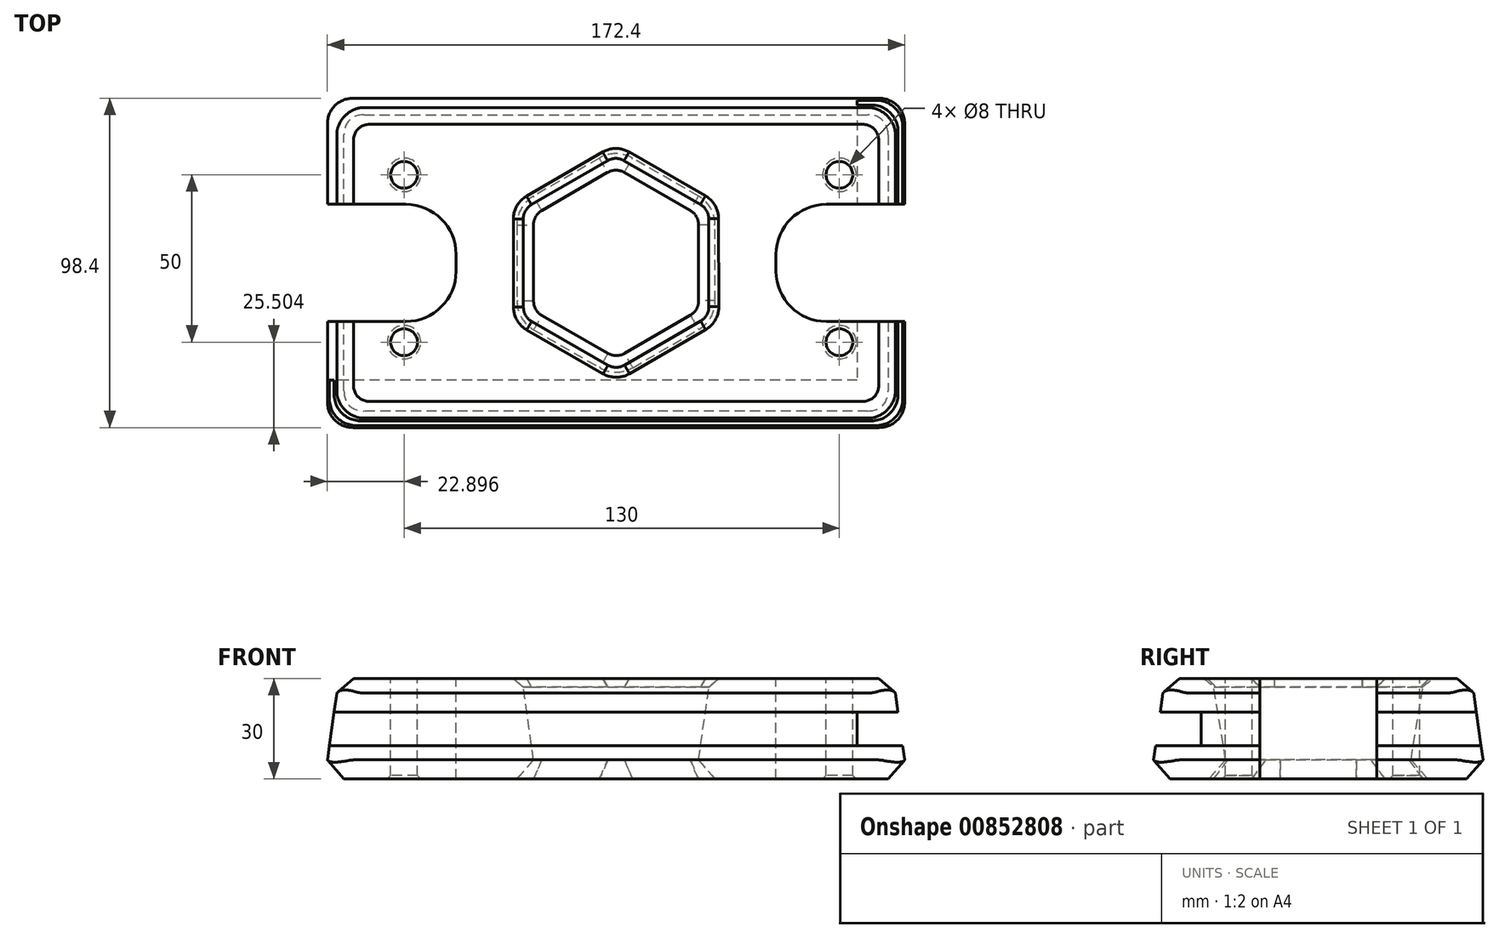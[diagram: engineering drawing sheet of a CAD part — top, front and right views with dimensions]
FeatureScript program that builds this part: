
annotation { "Feature Type Name" : "Feature", "Feature Type Description" : "" }
export const myFeature = defineFeature(function(context is Context, id is Id, definition is map)
    precondition{}
    {
        {
            var Q0;
            Q0=qCreatedBy(makeId("Top.planeOp"),FACE);
            var sketch = newSketch(context, id + "F0", { "sketchPlane" : qUnion([Q0])});
            skLineSegment(sketch, "E0.bottom", {"start": v(87, 50) * mm, "end": v(-87, 50) * mm});
            skLineSegment(sketch, "E0.top", {"start": v(87, -50) * mm, "end": v(-87, -50) * mm});
            skLineSegment(sketch, "E0.left", {"start": v(87, 50) * mm, "end": v(87, -50) * mm});
            skLineSegment(sketch, "E0.right", {"start": v(-87, 50) * mm, "end": v(-87, -50) * mm});
            skPoint(sketch, "E0.middle", {"position": v(0, 0) * mm});
            skCircle(sketch, "E1.cCircle", {"center": v(0, 0) * mm, "radius": 23.84 * mm, "construction": true});
            skLineSegment(sketch, "E1.0", {"start": v(-0.05, 27.52) * mm, "end": v(23.81, 13.8) * mm});
            skLineSegment(sketch, "E1.1", {"start": v(23.81, 13.8) * mm, "end": v(23.86, -13.72) * mm});
            skLineSegment(sketch, "E1.2", {"start": v(23.86, -13.72) * mm, "end": v(0.05, -27.52) * mm});
            skLineSegment(sketch, "E1.3", {"start": v(0.05, -27.52) * mm, "end": v(-23.81, -13.8) * mm});
            skLineSegment(sketch, "E1.4", {"start": v(-23.81, -13.8) * mm, "end": v(-23.86, 13.72) * mm});
            skLineSegment(sketch, "E1.5", {"start": v(-23.86, 13.72) * mm, "end": v(-0.05, 27.52) * mm});
            skPoint(sketch, "E1.0.midPoint", {"position": v(11.88, 20.66) * mm});
            skSolve(sketch);
        }
        {
            var Q0;
            Q0 = qSketchRegion(id + "F0", true);
            extrude(context, id + "F1", {"entities" : qUnion([Q0]), "depth" : 30 * mm, "offsetDistance" : 25 * mm, "hasDraft" : true, "draftAngle" : 8 * degree, "draftPullDirection" : true});
        }
        {
            var Q0;
            Q0=makeQuery(id+"F1.opExtrude","SWEPT_EDGE",EDGE,{"disambiguationData":[OSD([sQuery(id+"F0.wireOp",EDGE,"E1.4"),sQuery(id+"F0.wireOp",EDGE,"E1.5")])]});
            var Q1;
            Q1=makeQuery(id+"F1.opExtrude","SWEPT_EDGE",EDGE,{"disambiguationData":[OSD([sQuery(id+"F0.wireOp",EDGE,"E1.0"),sQuery(id+"F0.wireOp",EDGE,"E1.5")])]});
            var Q2;
            Q2=makeQuery(id+"F1.opExtrude","SWEPT_EDGE",EDGE,{"disambiguationData":[OSD([sQuery(id+"F0.wireOp",EDGE,"E1.0"),sQuery(id+"F0.wireOp",EDGE,"E1.1")])]});
            var Q3;
            Q3=makeQuery(id+"F1.opExtrude","SWEPT_EDGE",EDGE,{"disambiguationData":[OSD([sQuery(id+"F0.wireOp",EDGE,"E1.1"),sQuery(id+"F0.wireOp",EDGE,"E1.2")])]});
            var Q4;
            Q4=makeQuery(id+"F1.opExtrude","SWEPT_EDGE",EDGE,{"disambiguationData":[OSD([sQuery(id+"F0.wireOp",EDGE,"E1.2"),sQuery(id+"F0.wireOp",EDGE,"E1.3")])]});
            var Q5;
            Q5=makeQuery(id+"F1.opExtrude","SWEPT_EDGE",EDGE,{"disambiguationData":[OSD([sQuery(id+"F0.wireOp",EDGE,"E1.3"),sQuery(id+"F0.wireOp",EDGE,"E1.4")])]});
            fillet(context, id + "F2", {"entities" : qUnion([Q0, Q1, Q2, Q3, Q4, Q5]), "radius" : 5 * mm, "tangentPropagation" : true, "allowEdgeOverflow" : false});
        }
        {
            var Q0;
            Q0=makeQuery(id+"F1.opExtrude","CAP_EDGE",EDGE,{"disambiguationData":[OSD([sQuery(id+"F0.wireOp",EDGE,"E0.right")])],"isStart":false});
            var Q1;
            Q1=makeQuery(id+"F1.opExtrude","CAP_EDGE",EDGE,{"disambiguationData":[OSD([sQuery(id+"F0.wireOp",EDGE,"E0.top")])],"isStart":false});
            var Q2;
            Q2=makeQuery(id+"F1.opExtrude","CAP_EDGE",EDGE,{"disambiguationData":[OSD([sQuery(id+"F0.wireOp",EDGE,"E0.left")])],"isStart":false});
            var Q3;
            Q3=makeQuery(id+"F1.opExtrude","CAP_EDGE",EDGE,{"disambiguationData":[OSD([sQuery(id+"F0.wireOp",EDGE,"E0.bottom")])],"isStart":false});
            chamfer(context, id + "F3", {"entities" : qUnion([Q0, Q1, Q2, Q3]), "width" : 5 * mm, "tangentPropagation" : true});
        }
        {
            var Q0;
            Q0=makeQuery(id+"F1.opExtrude","CAP_EDGE",EDGE,{"disambiguationData":[OSD([sQuery(id+"F0.wireOp",EDGE,"E1.5")])],"isStart":false});
            chamfer(context, id + "F4", {"entities" : qUnion([Q0]), "width" : 3 * mm, "tangentPropagation" : true});
        }
        {
            var Q0;
            Q0=makeQuery(id+"F1.opExtrude","CAP_FACE",FACE,{"disambiguationData":[OSD([sQuery(id+"F0.wireOp",EDGE,"E0.bottom"),sQuery(id+"F0.wireOp",EDGE,"E0.top"),sQuery(id+"F0.wireOp",EDGE,"E0.left"),sQuery(id+"F0.wireOp",EDGE,"E0.right"),sQuery(id+"F0.wireOp",EDGE,"E1.0"),sQuery(id+"F0.wireOp",EDGE,"E1.1"),sQuery(id+"F0.wireOp",EDGE,"E1.2"),sQuery(id+"F0.wireOp",EDGE,"E1.3"),sQuery(id+"F0.wireOp",EDGE,"E1.4"),sQuery(id+"F0.wireOp",EDGE,"E1.5")])],"isStart":true});
            chamfer(context, id + "F5", {"entities" : qUnion([Q0]), "width" : 5 * mm, "tangentPropagation" : true});
        }
        {
            var Q0;
            Q0=makeQuery(id+"F1.opExtrude","SWEPT_EDGE",EDGE,{"disambiguationData":[OSD([sQuery(id+"F0.wireOp",EDGE,"E0.top"),sQuery(id+"F0.wireOp",EDGE,"E0.right")])]});
            var Q1;
            Q1=makeQuery(id+"F1.opExtrude","SWEPT_EDGE",EDGE,{"disambiguationData":[OSD([sQuery(id+"F0.wireOp",EDGE,"E0.top"),sQuery(id+"F0.wireOp",EDGE,"E0.left")])]});
            var Q2;
            Q2=makeQuery(id+"F1.opExtrude","SWEPT_EDGE",EDGE,{"disambiguationData":[OSD([sQuery(id+"F0.wireOp",EDGE,"E0.bottom"),sQuery(id+"F0.wireOp",EDGE,"E0.right")])]});
            var Q3;
            Q3=makeQuery(id+"F1.opExtrude","SWEPT_EDGE",EDGE,{"disambiguationData":[OSD([sQuery(id+"F0.wireOp",EDGE,"E0.bottom"),sQuery(id+"F0.wireOp",EDGE,"E0.left")])]});
            var Q4;
            Q4=makeQuery(id+"F3.opChamfer","BLEND_EDGE",EDGE,{"blendedFrom":[makeQuery(id+"F1.opExtrude","CAP_EDGE",EDGE,{"disambiguationData":[OSD([sQuery(id+"F0.wireOp",EDGE,"E0.top")])],"isStart":false}),makeQuery(id+"F1.opExtrude","CAP_EDGE",EDGE,{"disambiguationData":[OSD([sQuery(id+"F0.wireOp",EDGE,"E0.right")])],"isStart":false})],"blendedInto":[]});
            var Q5;
            Q5=makeQuery(id+"F3.opChamfer","BLEND_EDGE",EDGE,{"blendedFrom":[makeQuery(id+"F1.opExtrude","CAP_EDGE",EDGE,{"disambiguationData":[OSD([sQuery(id+"F0.wireOp",EDGE,"E0.top")])],"isStart":false}),makeQuery(id+"F1.opExtrude","CAP_EDGE",EDGE,{"disambiguationData":[OSD([sQuery(id+"F0.wireOp",EDGE,"E0.left")])],"isStart":false})],"blendedInto":[]});
            var Q6;
            Q6=makeQuery(id+"F3.opChamfer","BLEND_EDGE",EDGE,{"blendedFrom":[makeQuery(id+"F1.opExtrude","CAP_EDGE",EDGE,{"disambiguationData":[OSD([sQuery(id+"F0.wireOp",EDGE,"E0.bottom")])],"isStart":false}),makeQuery(id+"F1.opExtrude","CAP_EDGE",EDGE,{"disambiguationData":[OSD([sQuery(id+"F0.wireOp",EDGE,"E0.left")])],"isStart":false})],"blendedInto":[]});
            var Q7;
            Q7=makeQuery(id+"F5.opChamfer","BLEND_EDGE",EDGE,{"blendedFrom":[makeQuery(id+"F1.opExtrude","CAP_EDGE",EDGE,{"disambiguationData":[OSD([sQuery(id+"F0.wireOp",EDGE,"E0.top")])],"isStart":true}),makeQuery(id+"F1.opExtrude","CAP_EDGE",EDGE,{"disambiguationData":[OSD([sQuery(id+"F0.wireOp",EDGE,"E0.left")])],"isStart":true})],"blendedInto":[]});
            var Q8;
            Q8=makeQuery(id+"F5.opChamfer","BLEND_EDGE",EDGE,{"blendedFrom":[makeQuery(id+"F1.opExtrude","CAP_EDGE",EDGE,{"disambiguationData":[OSD([sQuery(id+"F0.wireOp",EDGE,"E0.top")])],"isStart":true}),makeQuery(id+"F1.opExtrude","CAP_EDGE",EDGE,{"disambiguationData":[OSD([sQuery(id+"F0.wireOp",EDGE,"E0.right")])],"isStart":true})],"blendedInto":[]});
            var Q9;
            Q9=makeQuery(id+"F5.opChamfer","BLEND_EDGE",EDGE,{"blendedFrom":[makeQuery(id+"F1.opExtrude","CAP_EDGE",EDGE,{"disambiguationData":[OSD([sQuery(id+"F0.wireOp",EDGE,"E0.bottom")])],"isStart":true}),makeQuery(id+"F1.opExtrude","CAP_EDGE",EDGE,{"disambiguationData":[OSD([sQuery(id+"F0.wireOp",EDGE,"E0.right")])],"isStart":true})],"blendedInto":[]});
            var Q10;
            Q10=makeQuery(id+"F5.opChamfer","BLEND_EDGE",EDGE,{"blendedFrom":[makeQuery(id+"F1.opExtrude","CAP_EDGE",EDGE,{"disambiguationData":[OSD([sQuery(id+"F0.wireOp",EDGE,"E0.bottom")])],"isStart":true}),makeQuery(id+"F1.opExtrude","CAP_EDGE",EDGE,{"disambiguationData":[OSD([sQuery(id+"F0.wireOp",EDGE,"E0.left")])],"isStart":true})],"blendedInto":[]});
            var Q11;
            Q11=makeQuery(id+"F3.opChamfer","BLEND_EDGE",EDGE,{"blendedFrom":[makeQuery(id+"F1.opExtrude","CAP_EDGE",EDGE,{"disambiguationData":[OSD([sQuery(id+"F0.wireOp",EDGE,"E0.bottom")])],"isStart":false}),makeQuery(id+"F1.opExtrude","CAP_EDGE",EDGE,{"disambiguationData":[OSD([sQuery(id+"F0.wireOp",EDGE,"E0.right")])],"isStart":false})],"blendedInto":[]});
            fillet(context, id + "F6", {"entities" : qUnion([Q0, Q1, Q2, Q3, Q4, Q5, Q6, Q7, Q8, Q9, Q10, Q11]), "radius" : 8 * mm, "tangentPropagation" : true, "allowEdgeOverflow" : false});
        }
        {
            var Q0;
            Q0=makeQuery(id+"F1.opExtrude","CAP_FACE",FACE,{"disambiguationData":[OSD([sQuery(id+"F0.wireOp",EDGE,"E0.bottom"),sQuery(id+"F0.wireOp",EDGE,"E0.top"),sQuery(id+"F0.wireOp",EDGE,"E0.left"),sQuery(id+"F0.wireOp",EDGE,"E0.right"),sQuery(id+"F0.wireOp",EDGE,"E1.0"),sQuery(id+"F0.wireOp",EDGE,"E1.1"),sQuery(id+"F0.wireOp",EDGE,"E1.2"),sQuery(id+"F0.wireOp",EDGE,"E1.3"),sQuery(id+"F0.wireOp",EDGE,"E1.4"),sQuery(id+"F0.wireOp",EDGE,"E1.5")])],"isStart":false});
            var sketch = newSketch(context, id + "F7", { "sketchPlane" : qUnion([Q0])});
            skLineSegment(sketch, "E2.bottom", {"start": v(107.78, 17.5) * mm, "end": v(47.78, 17.5) * mm});
            skLineSegment(sketch, "E2.top", {"start": v(107.78, -17.5) * mm, "end": v(47.78, -17.5) * mm});
            skLineSegment(sketch, "E2.left", {"start": v(107.78, 17.5) * mm, "end": v(107.78, -17.5) * mm});
            skLineSegment(sketch, "E2.right", {"start": v(47.78, 17.5) * mm, "end": v(47.78, -17.5) * mm});
            skPoint(sketch, "E2.middle", {"position": v(77.78, 0) * mm});
            skLineSegment(sketch, "E3.bottom", {"start": v(-107.78, 17.5) * mm, "end": v(-47.78, 17.5) * mm});
            skLineSegment(sketch, "E3.top", {"start": v(-107.78, -17.5) * mm, "end": v(-47.78, -17.5) * mm});
            skLineSegment(sketch, "E3.left", {"start": v(-107.78, 17.5) * mm, "end": v(-107.78, -17.5) * mm});
            skLineSegment(sketch, "E3.right", {"start": v(-47.78, 17.5) * mm, "end": v(-47.78, -17.5) * mm});
            skPoint(sketch, "E3.middle", {"position": v(-77.78, 0) * mm});
            skSolve(sketch);
        }
        {
            var Q0;
            Q0 = qSketchRegion(id + "F7", true);
            extrude(context, id + "F8", {"entities" : qUnion([Q0]), "operationType" : NewBodyOperationType.REMOVE, "endBound" : BoundingType.THROUGH_ALL, "oppositeDirection" : true, "depth" : 25 * mm, "offsetDistance" : 25 * mm});
        }
        {
            var Q0;
            Q0=makeQuery(id+"F8.boolean.opBoolean","COPY",EDGE,{"derivedFrom":makeQuery(id+"F8.opExtrude","SWEPT_EDGE",EDGE,{"disambiguationData":[OSD([sQuery(id+"F7.wireOp",EDGE,"E3.bottom"),sQuery(id+"F7.wireOp",EDGE,"E3.right")])]})});
            var Q1;
            Q1=makeQuery(id+"F8.boolean.opBoolean","COPY",EDGE,{"derivedFrom":makeQuery(id+"F8.opExtrude","SWEPT_EDGE",EDGE,{"disambiguationData":[OSD([sQuery(id+"F7.wireOp",EDGE,"E3.top"),sQuery(id+"F7.wireOp",EDGE,"E3.right")])]})});
            var Q2;
            Q2=makeQuery(id+"F8.boolean.opBoolean","COPY",EDGE,{"derivedFrom":makeQuery(id+"F8.opExtrude","SWEPT_EDGE",EDGE,{"disambiguationData":[OSD([sQuery(id+"F7.wireOp",EDGE,"E2.top"),sQuery(id+"F7.wireOp",EDGE,"E2.right")])]})});
            var Q3;
            Q3=makeQuery(id+"F8.boolean.opBoolean","COPY",EDGE,{"derivedFrom":makeQuery(id+"F8.opExtrude","SWEPT_EDGE",EDGE,{"disambiguationData":[OSD([sQuery(id+"F7.wireOp",EDGE,"E2.bottom"),sQuery(id+"F7.wireOp",EDGE,"E2.right")])]})});
            fillet(context, id + "F9", {"entities" : qUnion([Q0, Q1, Q2, Q3]), "radius" : 15 * mm, "tangentPropagation" : true, "allowEdgeOverflow" : false});
        }
        {
            var Q0;
            Q0=makeQuery(id+"F1.opExtrude","CAP_FACE",FACE,{"disambiguationData":[OSD([sQuery(id+"F0.wireOp",EDGE,"E0.bottom"),sQuery(id+"F0.wireOp",EDGE,"E0.top"),sQuery(id+"F0.wireOp",EDGE,"E0.left"),sQuery(id+"F0.wireOp",EDGE,"E0.right"),sQuery(id+"F0.wireOp",EDGE,"E1.0"),sQuery(id+"F0.wireOp",EDGE,"E1.1"),sQuery(id+"F0.wireOp",EDGE,"E1.2"),sQuery(id+"F0.wireOp",EDGE,"E1.3"),sQuery(id+"F0.wireOp",EDGE,"E1.4"),sQuery(id+"F0.wireOp",EDGE,"E1.5")])],"isStart":false});
            var sketch = newSketch(context, id + "F10", { "sketchPlane" : qUnion([Q0])});
            skCircle(sketch, "E4", {"center": v(-63.3, 26.3) * mm, "radius": 4 * mm});
            skLineSegment(sketch, "E5", {"start": v(0, 0) * mm, "end": v(0, 5.87) * mm, "construction": true});
            skCircle(sketch, "E6.0.1.0", {"center": v(-63.3, -23.7) * mm, "radius": 4 * mm});
            skCircle(sketch, "E6.1.0.0", {"center": v(66.7, 26.3) * mm, "radius": 4 * mm});
            skCircle(sketch, "E6.1.1.0", {"center": v(66.7, -23.7) * mm, "radius": 4 * mm});
            skLineSegment(sketch, "E6.direction1", {"start": v(-63.3, 26.3) * mm, "end": v(66.7, 26.3) * mm, "construction": true});
            skLineSegment(sketch, "E6.direction2", {"start": v(-63.3, 26.3) * mm, "end": v(-63.3, -23.7) * mm, "construction": true});
            skSolve(sketch);
        }
        {
            var Q0;
            Q0 = qSketchRegion(id + "F10", true);
            extrude(context, id + "F11", {"entities" : qUnion([Q0]), "operationType" : NewBodyOperationType.REMOVE, "endBound" : BoundingType.THROUGH_ALL, "oppositeDirection" : true, "depth" : 25 * mm, "offsetDistance" : 25 * mm});
        }
        {
            var Q0;
            Q0=makeQuery(id+"F11.boolean.opBoolean","COPY",EDGE,{"derivedFrom":makeQuery(id+"F11.opExtrude","CAP_EDGE",EDGE,{"disambiguationData":[OSD([sQuery(id+"F10.wireOp",EDGE,"E4")])],"isStart":true})});
            var Q1;
            Q1=makeQuery(id+"F11.boolean.opBoolean","COPY",EDGE,{"derivedFrom":makeQuery(id+"F11.opExtrude","CAP_EDGE",EDGE,{"disambiguationData":[OSD([sQuery(id+"F10.wireOp",EDGE,"E6.0.1.0")])],"isStart":true})});
            var Q2;
            Q2=makeQuery(id+"F11.boolean.opBoolean","COPY",EDGE,{"derivedFrom":makeQuery(id+"F11.opExtrude","CAP_EDGE",EDGE,{"disambiguationData":[OSD([sQuery(id+"F10.wireOp",EDGE,"E6.1.0.0")])],"isStart":true})});
            var Q3;
            Q3=makeQuery(id+"F11.boolean.opBoolean","COPY",EDGE,{"derivedFrom":makeQuery(id+"F11.opExtrude","CAP_EDGE",EDGE,{"disambiguationData":[OSD([sQuery(id+"F10.wireOp",EDGE,"E6.1.1.0")])],"isStart":true})});
            var Q4;
            Q4=makeQuery(id+"F11.boolean.opBoolean","INTERSECT",EDGE,{"derivedFrom":[makeQuery(id+"F1.opExtrude","CAP_FACE",FACE,{"disambiguationData":[OSD([sQuery(id+"F0.wireOp",EDGE,"E0.bottom"),sQuery(id+"F0.wireOp",EDGE,"E0.top"),sQuery(id+"F0.wireOp",EDGE,"E0.left"),sQuery(id+"F0.wireOp",EDGE,"E0.right"),sQuery(id+"F0.wireOp",EDGE,"E1.0"),sQuery(id+"F0.wireOp",EDGE,"E1.1"),sQuery(id+"F0.wireOp",EDGE,"E1.2"),sQuery(id+"F0.wireOp",EDGE,"E1.3"),sQuery(id+"F0.wireOp",EDGE,"E1.4"),sQuery(id+"F0.wireOp",EDGE,"E1.5")])],"isStart":true}),makeQuery(id+"F11.opExtrude","SWEPT_FACE",FACE,{"disambiguationData":[OSD([sQuery(id+"F10.wireOp",EDGE,"E6.0.1.0")])]})]});
            var Q5;
            Q5=makeQuery(id+"F11.boolean.opBoolean","INTERSECT",EDGE,{"derivedFrom":[makeQuery(id+"F1.opExtrude","CAP_FACE",FACE,{"disambiguationData":[OSD([sQuery(id+"F0.wireOp",EDGE,"E0.bottom"),sQuery(id+"F0.wireOp",EDGE,"E0.top"),sQuery(id+"F0.wireOp",EDGE,"E0.left"),sQuery(id+"F0.wireOp",EDGE,"E0.right"),sQuery(id+"F0.wireOp",EDGE,"E1.0"),sQuery(id+"F0.wireOp",EDGE,"E1.1"),sQuery(id+"F0.wireOp",EDGE,"E1.2"),sQuery(id+"F0.wireOp",EDGE,"E1.3"),sQuery(id+"F0.wireOp",EDGE,"E1.4"),sQuery(id+"F0.wireOp",EDGE,"E1.5")])],"isStart":true}),makeQuery(id+"F11.opExtrude","SWEPT_FACE",FACE,{"disambiguationData":[OSD([sQuery(id+"F10.wireOp",EDGE,"E4")])]})]});
            var Q6;
            Q6=makeQuery(id+"F11.boolean.opBoolean","INTERSECT",EDGE,{"derivedFrom":[makeQuery(id+"F1.opExtrude","CAP_FACE",FACE,{"disambiguationData":[OSD([sQuery(id+"F0.wireOp",EDGE,"E0.bottom"),sQuery(id+"F0.wireOp",EDGE,"E0.top"),sQuery(id+"F0.wireOp",EDGE,"E0.left"),sQuery(id+"F0.wireOp",EDGE,"E0.right"),sQuery(id+"F0.wireOp",EDGE,"E1.0"),sQuery(id+"F0.wireOp",EDGE,"E1.1"),sQuery(id+"F0.wireOp",EDGE,"E1.2"),sQuery(id+"F0.wireOp",EDGE,"E1.3"),sQuery(id+"F0.wireOp",EDGE,"E1.4"),sQuery(id+"F0.wireOp",EDGE,"E1.5")])],"isStart":true}),makeQuery(id+"F11.opExtrude","SWEPT_FACE",FACE,{"disambiguationData":[OSD([sQuery(id+"F10.wireOp",EDGE,"E6.1.0.0")])]})]});
            var Q7;
            Q7=makeQuery(id+"F11.boolean.opBoolean","INTERSECT",EDGE,{"derivedFrom":[makeQuery(id+"F1.opExtrude","CAP_FACE",FACE,{"disambiguationData":[OSD([sQuery(id+"F0.wireOp",EDGE,"E0.bottom"),sQuery(id+"F0.wireOp",EDGE,"E0.top"),sQuery(id+"F0.wireOp",EDGE,"E0.left"),sQuery(id+"F0.wireOp",EDGE,"E0.right"),sQuery(id+"F0.wireOp",EDGE,"E1.0"),sQuery(id+"F0.wireOp",EDGE,"E1.1"),sQuery(id+"F0.wireOp",EDGE,"E1.2"),sQuery(id+"F0.wireOp",EDGE,"E1.3"),sQuery(id+"F0.wireOp",EDGE,"E1.4"),sQuery(id+"F0.wireOp",EDGE,"E1.5")])],"isStart":true}),makeQuery(id+"F11.opExtrude","SWEPT_FACE",FACE,{"disambiguationData":[OSD([sQuery(id+"F10.wireOp",EDGE,"E6.1.1.0")])]})]});
            chamfer(context, id + "F12", {"entities" : qUnion([Q0, Q1, Q2, Q3, Q4, Q5, Q6, Q7]), "width" : 1 * mm, "tangentPropagation" : true});
        }
        {
            var Q0;
            Q0=qCreatedBy(makeId("Front.planeOp"),FACE);
            cPlane(context, id + "F13", {"entities" : qUnion([Q0]), "cplaneType" : CPlaneType.OFFSET, "offset" : 60 * mm, "width" : 150 * mm, "height" : 150 * mm});
        }
        {
            var Q0;
            Q0=qCreatedBy(id+"F13.planeOp",FACE);
            var sketch = newSketch(context, id + "F14", { "sketchPlane" : qUnion([Q0])});
            skLineSegment(sketch, "E7", {"start": v(0, 0) * mm, "end": v(0, 30) * mm, "construction": true});
            skLineSegment(sketch, "E8.bottom", {"start": v(100, 20) * mm, "end": v(-100, 20) * mm});
            skLineSegment(sketch, "E8.top", {"start": v(100, 10) * mm, "end": v(-100, 10) * mm});
            skLineSegment(sketch, "E8.left", {"start": v(100, 20) * mm, "end": v(100, 10) * mm});
            skLineSegment(sketch, "E8.right", {"start": v(-100, 20) * mm, "end": v(-100, 10) * mm});
            skPoint(sketch, "E8.middle", {"position": v(0, 15) * mm});
            skSolve(sketch);
        }
        {
            var Q0;
            Q0 = qSketchRegion(id + "F14", true);
            extrude(context, id + "F15", {"entities" : qUnion([Q0]), "operationType" : NewBodyOperationType.REMOVE, "oppositeDirection" : true, "depth" : 25 * mm, "offsetDistance" : 25 * mm});
        }
        {
            var Q0;
            Q0=qCreatedBy(makeId("Right.planeOp"),FACE);
            cPlane(context, id + "F16", {"entities" : qUnion([Q0]), "cplaneType" : CPlaneType.OFFSET, "offset" : 100 * mm, "width" : 150 * mm, "height" : 150 * mm});
        }
        {
            var Q0;
            Q0=qCreatedBy(id+"F16.planeOp",FACE);
            var sketch = newSketch(context, id + "F17", { "sketchPlane" : qUnion([Q0])});
            skLineSegment(sketch, "E9", {"start": v(0, 0) * mm, "end": v(0, 30) * mm, "construction": true});
            skLineSegment(sketch, "E10.bottom", {"start": v(62.5, 20) * mm, "end": v(-62.5, 20) * mm});
            skLineSegment(sketch, "E10.top", {"start": v(62.5, 10) * mm, "end": v(-62.5, 10) * mm});
            skLineSegment(sketch, "E10.left", {"start": v(62.5, 20) * mm, "end": v(62.5, 10) * mm});
            skLineSegment(sketch, "E10.right", {"start": v(-62.5, 20) * mm, "end": v(-62.5, 10) * mm});
            skPoint(sketch, "E10.middle", {"position": v(0, 15) * mm});
            skSolve(sketch);
        }
        {
            var Q0;
            Q0 = qSketchRegion(id + "F17", true);
            extrude(context, id + "F18", {"entities" : qUnion([Q0]), "operationType" : NewBodyOperationType.REMOVE, "oppositeDirection" : true, "depth" : 28 * mm, "offsetDistance" : 25 * mm});
        }
    });
